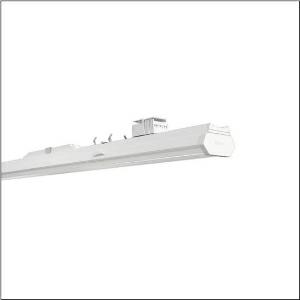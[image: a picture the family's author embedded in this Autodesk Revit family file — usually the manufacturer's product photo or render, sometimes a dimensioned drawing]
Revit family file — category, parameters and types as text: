
# Revit family: licross_r__11_protected_mo_51tp11mn495g_eae0
name_source: partatom
category: Lighting Fixtures
units: mm (PartAtom-declared; Revit-internal decimal feet)

## family parameters
Cut with Voids When Loaded = No
Host = Face
Light Source = No
Part Type = Normal
Room Calculation Point = No
Round Connector Dimension = Use Diameter
Shared = No

## types (1)
- --- (1 x LED, 9980 lm, 55.3 W, 4000K)
    Apparent Load = 55 VA
    CIE Flux Codes = 83 94 98 100 100
    Color Rendering = 80
    Color Temperature = 4000K
    Default Elevation = 1800 mm
    Description = Licross® 11 Protected MO, luminaire insert, of sheet steel, galvanised, coil coated, white, length: 1.500mm, width: 90mm, height: 101mm, LED rated luminous flux: 9.980lm, light colour: 840, control gear: ON/OFF Multilumen, control gear: ECG Multilumen, with plug, 3-pole, with phase selection, mains connection: 220..240V, AC, 50/60Hz, halogen-free wiring, primary light control with lens, of plastic, primary optical cover: cover, of PMMA, light emission: direct with ceiling illumination distribution, primary light characteristic: symmetric, protection rating (complete): IP64, insulation class (complete): insulation class I (protective earthing), certification: CE, ENEC, VDE, UKCA, protection symbol: D if used in an environment with conductive dust loads with corresponding accessories, impact resistance: IK06, permissible ambient temperature for indoor applications: -35..+40°C, corresponds to IFS (International Featured Standards) requirements for safety and quality in the food industry, reducing of maximum allowable ambient temperature of 5°C with ceiling mounting, LABS conformity tested according to VDMA 24364:2018-05, packaging unit: 1 piece
    Height = 92 mm
    Lamp = 1 x LED
    Lamp Light Flux = 9980 lm
    Lamp Power = 55.3 W
    Lamp count = 1
    Length = 1500 mm
    Luminous efficacy = 180 lm/W
    Manufacturer = Siteco
    ModVariant = No
    Model = 51TP11MN495G
    Mounting Place = Ceiling
    Mounting Type = Pendant
    Number of Poles = 1
    OnlyDefault = Yes
    Power Factor = 1
    Product Name = Licross® 11 Protected MO
    Product group = luminaire insert
    ProductGroupID = 902
    Protection Class = Protection class I
    Protection Degree = IP 64
    RLX_Detail_Level = 1
    RlxData = <blob elided: 21837 chars, md5=cf303af4>
    Socket = socket
    Standby Power = 0 W
    System Light Flux = 9980 lm
    System Power = 55 W
    Type Comments = factory setting: luminous flux: 100 % | (A | C | E) | 126 mA
    Type Image = l_1256148.jpg
    URL = http://relux.com
    VarID = @adj_003721
    Voltage = 0 V
    Weight = 0.00 kg
    Width = 88 mm

## geometry (parser evidence)
native form markers: Blend x4, Sweep x11
no freeform markers — native parametric forms only
